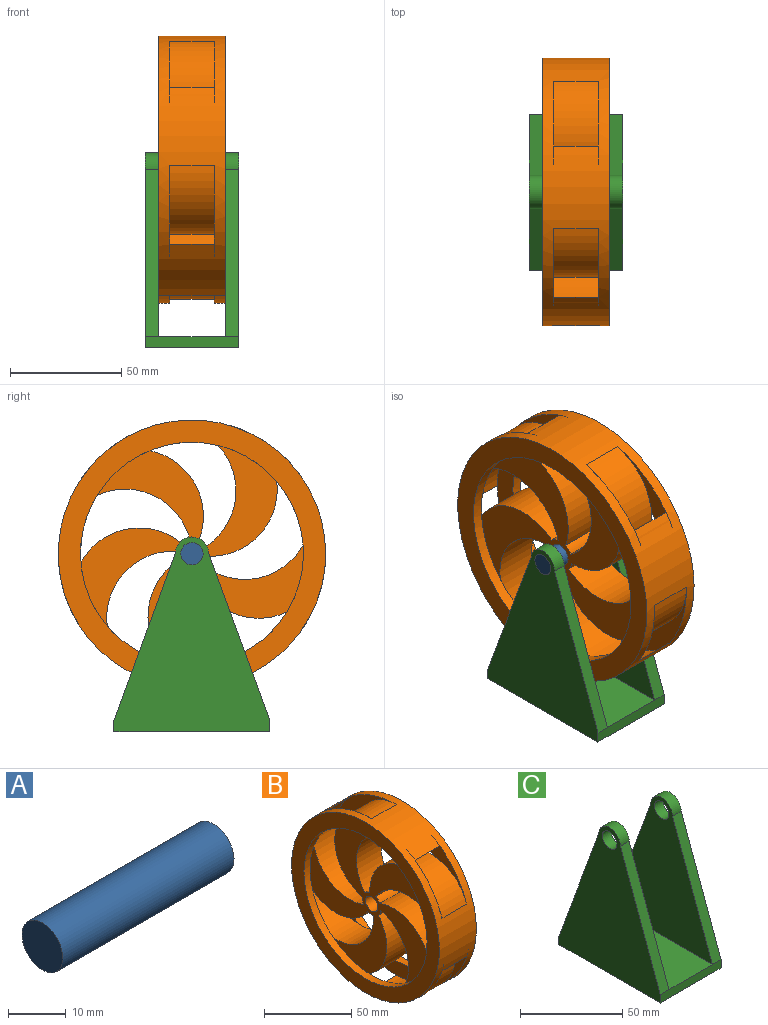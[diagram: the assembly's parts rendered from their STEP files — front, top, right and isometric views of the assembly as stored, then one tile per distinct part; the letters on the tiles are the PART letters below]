
ASSEMBLY  parts=3 mates=2
PART A: 3 faces, bbox 42x10x10 mm
  f0: cylinder r=5mm len=42mm, axis (-1,0,0), area 1319.5mm2, adj f1,f2
  f1: plane 10x10mm, normal (1,0,0), area 78.5mm2, adj f0
  f2: plane 10x10mm, normal (-1,0,0), area 78.5mm2, adj f0
PART B: 35 faces, bbox 30x120x120 mm
  f0: plane 99.95x98.17mm, normal (1,0,0), area 3936.8mm2, adj f2,f3,f4,f5,f6,f7,f8,f9
  f1: plane 99.95x98.17mm, normal (-1,0,0), area 3936.8mm2, adj f2,f3,f4,f5,f6,f7,f8,f9
  f2: cylinder r=30mm len=49.14mm, axis (-1,0,0), area 1734.6mm2, adj f0,f1,f3,f14,f19,f27
  f3: cylinder r=7.5mm len=20mm, axis (-1,0,0), area 94.2mm2, adj f0,f1,f2,f4
  f4: cylinder r=30mm len=58.53mm, axis (-1,0,0), area 1734.6mm2, adj f0,f1,f3,f14,f19,f27
  f5: cylinder r=30mm len=55.34mm, axis (-1,0,0), area 1734.6mm2, adj f0,f1,f6,f14,f23,f28
  f6: cylinder r=7.5mm len=20mm, axis (-1,0,0), area 94.2mm2, adj f0,f1,f5,f7
  f7: cylinder r=30mm len=54.27mm, axis (-1,0,0), area 1734.6mm2, adj f0,f1,f6,f14,f23,f28
  f8: cylinder r=30mm len=59.06mm, axis (-1,0,0), area 1734.6mm2, adj f0,f1,f9,f14,f22,f29
  f9: cylinder r=7.5mm len=20mm, axis (-1,0,0), area 94.2mm2, adj f0,f1,f8,f10
  f10: cylinder r=30mm len=49.14mm, axis (-1,0,0), area 1734.6mm2, adj f0,f1,f9,f14,f22,f29
  f11: cylinder r=30mm len=58.53mm, axis (-1,0,0), area 1734.6mm2, adj f0,f1,f12,f14,f21,f30
  f12: cylinder r=7.5mm len=20mm, axis (-1,0,0), area 94.2mm2, adj f0,f1,f11,f13
  f13: cylinder r=30mm len=55.34mm, axis (-1,0,0), area 1734.6mm2, adj f0,f1,f12,f14,f21,f30
  f14: cylinder r=60mm len=120mm, axis (-1,0,0), area 7162.8mm2, adj f2,f4,f5,f7,f8,f10,f11,f13
  f15: cylinder r=30mm len=54.27mm, axis (-1,0,0), area 1734.6mm2, adj f0,f1,f14,f16,f20,f34
  f16: cylinder r=7.5mm len=20mm, axis (-1,0,0), area 94.2mm2, adj f0,f1,f15,f17
  f17: cylinder r=30mm len=59.06mm, axis (-1,0,0), area 1734.6mm2, adj f0,f1,f14,f16,f20,f34
  f18: cylinder r=5mm len=20mm, axis (-1,0,0), area 628.3mm2, adj f0,f1
  f19: plane 54.93x35.73mm, normal (1,0,0), area 345.6mm2, adj f2,f4,f14,f25
  f20: plane 47.63x42.54mm, normal (1,0,0), area 345.6mm2, adj f14,f15,f17,f25
  f21: plane 57.7x28.91mm, normal (1,0,0), area 345.6mm2, adj f11,f13,f24,f25
  f22: plane 62.91x18.33mm, normal (1,0,0), area 345.6mm2, adj f8,f10,f14,f25
  f23: plane 61.95x23.26mm, normal (1,0,0), area 345.6mm2, adj f5,f7,f14,f25
  f24: extruded ~37.08x5mm, area 188.5mm2, adj f14,f21,f26
  f25: cylinder r=50mm len=100mm, axis (1,0,0), area 1570.8mm2, adj f1,f19,f20,f21,f22,f23,f26
  f26: plane 120x120mm, normal (-1,0,0), area 3455.7mm2, adj f14,f24,f25
  f27: plane 54.93x35.73mm, normal (-1,0,0), area 345.6mm2, adj f2,f4,f14,f32
  f28: plane 61.95x23.26mm, normal (-1,0,0), area 345.6mm2, adj f5,f7,f14,f32
  f29: plane 62.91x18.33mm, normal (-1,0,0), area 345.6mm2, adj f8,f10,f14,f32
  f30: plane 57.7x28.91mm, normal (-1,0,0), area 345.6mm2, adj f11,f13,f31,f32
  f31: extruded ~37.08x5mm, area 188.5mm2, adj f14,f30,f33
  f32: cylinder r=50mm len=100mm, axis (-1,0,0), area 1570.8mm2, adj f0,f27,f28,f29,f30,f33,f34
  f33: plane 120x120mm, normal (1,0,0), area 3455.7mm2, adj f14,f31,f32
  f34: plane 47.63x42.54mm, normal (-1,0,0), area 345.6mm2, adj f14,f15,f17,f32
PART C: 16 faces, bbox 42x70x87.5 mm
  f0: plane 75x27.5mm, normal (0,0.94,0.34), area 479.3mm2, adj f1,f4,f5,f14
  f1: cylinder r=7.5mm len=15mm, axis (-1,0,0), area 141.4mm2, adj f0,f2,f4,f5
  f2: plane 75x27.5mm, normal (0,-0.94,0.34), area 479.3mm2, adj f1,f4,f5,f13
  f3: cylinder r=5mm len=10mm, axis (-1,0,0), area 188.5mm2, adj f4,f5
  f4: plane 87.5x70mm, normal (1,0,0), area 3547.3mm2, adj f0,f1,f2,f3,f13,f14,f15
  f5: plane 82.5x70mm, normal (-1,0,0), area 3197.3mm2, adj f0,f1,f2,f3,f6
  f6: plane 70x30mm, normal (0,0,1), area 2100mm2, adj f5,f12,f13,f14
  f7: plane 75x27.5mm, normal (0,0.94,0.34), area 479.3mm2, adj f8,f11,f12,f14
  f8: cylinder r=7.5mm len=15mm, axis (1,0,0), area 141.4mm2, adj f7,f9,f11,f12
  f9: plane 75x27.5mm, normal (0,-0.94,0.34), area 479.3mm2, adj f8,f11,f12,f13
  f10: cylinder r=5mm len=10mm, axis (1,0,0), area 188.5mm2, adj f11,f12
  f11: plane 87.5x70mm, normal (-1,0,0), area 3547.3mm2, adj f7,f8,f9,f10,f13,f14,f15
  f12: plane 82.5x70mm, normal (1,0,0), area 3197.3mm2, adj f6,f7,f8,f9,f10
  f13: plane 42x5mm, normal (0,-1,0), area 210mm2, adj f2,f4,f6,f9,f11,f15
  f14: plane 42x5mm, normal (0,1,0), area 210mm2, adj f0,f4,f6,f7,f11,f15
  f15: plane 70x42mm, normal (0,0,-1), area 2940mm2, adj f4,f11,f13,f14
PLACE A t=(0,0,75)mm
PLACE B rot(axis=(0,-0.69,0.72),180deg) t=(0,0,75)mm
PLACE C t=(0,0,75)mm
MATE fastened A.f0 <-> C.f3  axis (1,0,0) through (21,0,75)mm
MATE revolute B.f18 <-> A.f0  axis (1,0,0) through (0,0,75)mm
